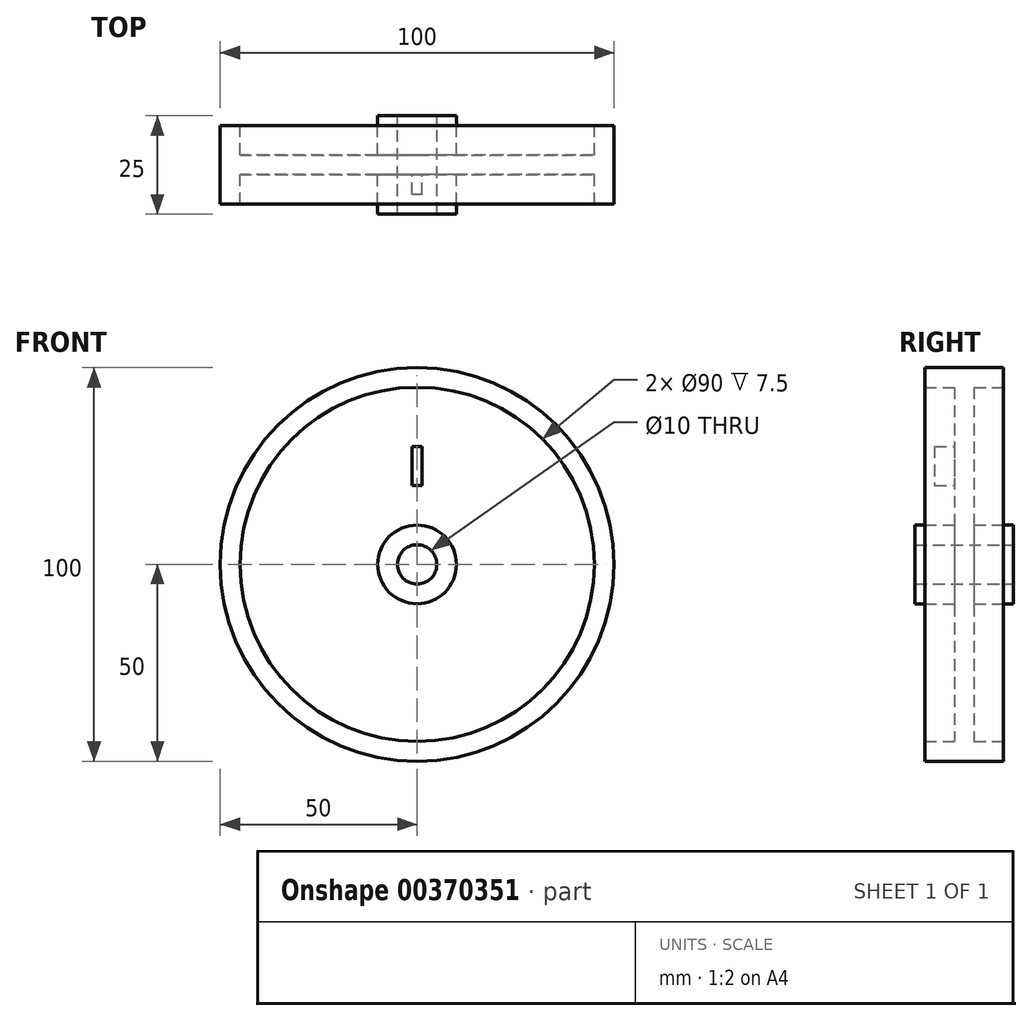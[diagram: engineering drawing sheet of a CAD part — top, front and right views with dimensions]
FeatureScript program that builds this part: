
annotation { "Feature Type Name" : "Feature", "Feature Type Description" : "" }
export const myFeature = defineFeature(function(context is Context, id is Id, definition is map)
    precondition{}
    {
        {
            var Q0;
            Q0=qCreatedBy(makeId("Right.planeOp"),FACE);
            var sketch = newSketch(context, id + "F0", { "sketchPlane" : qUnion([Q0])});
            skLineSegment(sketch, "E0", {"start": v(0, 5) * mm, "end": v(-25, 5) * mm});
            skLineSegment(sketch, "E1", {"start": v(-25, 5) * mm, "end": v(-25, 10) * mm});
            skLineSegment(sketch, "E2", {"start": v(-25, 10) * mm, "end": v(-15, 10) * mm});
            skLineSegment(sketch, "E3", {"start": v(-15, 10) * mm, "end": v(-15, 45) * mm});
            skLineSegment(sketch, "E4", {"start": v(-15, 45) * mm, "end": v(-22.5, 45) * mm});
            skLineSegment(sketch, "E5", {"start": v(-22.5, 50) * mm, "end": v(-2.5, 50) * mm});
            skLineSegment(sketch, "E6", {"start": v(-2.5, 45) * mm, "end": v(-10, 45) * mm});
            skLineSegment(sketch, "E7", {"start": v(-10, 45) * mm, "end": v(-10, 10) * mm});
            skLineSegment(sketch, "E8", {"start": v(-10, 10) * mm, "end": v(0, 10) * mm});
            skLineSegment(sketch, "E9", {"start": v(0, 10) * mm, "end": v(0, 5) * mm});
            skLineSegment(sketch, "E10", {"start": v(-2.5, 45) * mm, "end": v(-2.5, 50) * mm});
            skLineSegment(sketch, "E11", {"start": v(-22.5, 50) * mm, "end": v(-22.5, 45) * mm});
            skPoint(sketch, "E12.orphan", {"position": v(-25, 45) * mm});
            skPoint(sketch, "E13.end.orphan", {"position": v(0, 45) * mm});
            skPoint(sketch, "E14.orphan", {"position": v(0, 50) * mm});
            skSolve(sketch);
        }
        {
            var Q0;
            Q0=qCreatedBy(makeId("Right.planeOp"),FACE);
            var sketch = newSketch(context, id + "F1", { "sketchPlane" : qUnion([Q0])});
            skLineSegment(sketch, "E15", {"start": v(0, 0) * mm, "end": v(-47.85, 0) * mm});
            skSolve(sketch);
        }
        {
            var Q0;
            Q0=makeQuery(id+"F0.imprint","IMPRINT",FACE,{"disambiguationData":[TD([[makeQuery(id+"F0.imprint","IMPRINT",EDGE,{"derivedFrom":sQuery(id+"F0.wireOp",EDGE,"E0")}),-1.0]])]});
            var Q1;
            Q1=sQuery(id+"F1.wireOp",EDGE,"E15");
            revolve(context, id + "F2", {"entities" : qUnion([Q0]), "axis" : qUnion([Q1]), "revolveType" : RevolveType.FULL});
        }
        {
            var Q0;
            Q0=makeQuery(id+"F2.opRevolve","SWEPT_FACE",FACE,{"disambiguationData":[OSD([sQuery(id+"F0.wireOp",EDGE,"E3")])]});
            var sketch = newSketch(context, id + "F3", { "sketchPlane" : qUnion([Q0])});
            skLineSegment(sketch, "E16.bottom", {"start": v(1.25, 30) * mm, "end": v(-1.25, 30) * mm});
            skLineSegment(sketch, "E16.top", {"start": v(1.25, 20) * mm, "end": v(-1.25, 20) * mm});
            skLineSegment(sketch, "E16.left", {"start": v(1.25, 30) * mm, "end": v(1.25, 20) * mm});
            skLineSegment(sketch, "E16.right", {"start": v(-1.25, 30) * mm, "end": v(-1.25, 20) * mm});
            skPoint(sketch, "E16.middle", {"position": v(0, 25) * mm});
            skSolve(sketch);
        }
        {
            var Q0;
            Q0=makeQuery(id+"F3.imprint","IMPRINT",FACE,{"disambiguationData":[TD([[makeQuery(id+"F3.imprint","IMPRINT",EDGE,{"derivedFrom":sQuery(id+"F3.wireOp",EDGE,"E16.bottom")}),1.0]])]});
            extrude(context, id + "F4", {"entities" : qUnion([Q0]), "operationType" : NewBodyOperationType.ADD, "depth" : 5 * mm});
        }
    });
